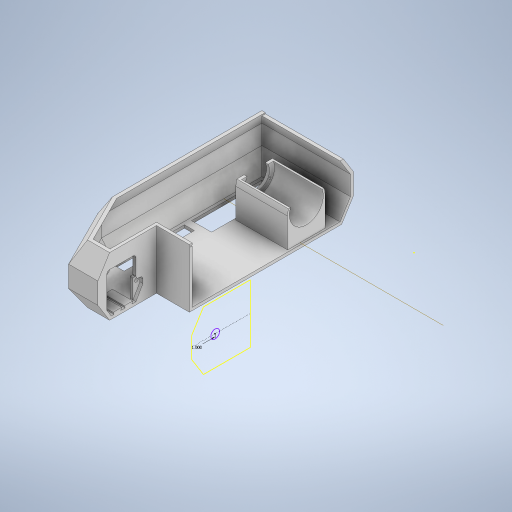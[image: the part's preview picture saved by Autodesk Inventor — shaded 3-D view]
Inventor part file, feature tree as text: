
AUTODESK INVENTOR PART (.ipt)
format: ipt  version: 2024 (Build 280153000, 153)  size: 1,161,216 bytes
history: native  units: in
note: dims shown in document units (in); Inventor stores cm internally (conversion verified against a paired STEP export)
features: extrude x14, sketch x13, projected_geometry x12, fillet x3, chamfer x2, shell x1, other x1, plane x1, mirror x1, hole x1
ambient origin geometry x8: Origin, YZ Plane, XZ Plane, XY Plane, X Axis, Y Axis, Z Axis, Center Point
bodies: Solid1 (feature_tree)
feature tree (49):
  extrude  "Extrusion1"  Depth=0.8in
  chamfer  "Chamfer1"  Distance=2.5in
  chamfer  "Chamfer2"  Distance=0.5in Angle=30.0deg
  shell  "Shell1"  Thickness=0.125in
  extrude  "Extrusion2"  Depth=3.0in
  extrude  "Extrusion3"  Depth=0.125in
  sketch  "Sketch4"  dims[d17=3.0in d18=0.125in]
  extrude  "Extrusion4"  Depth=0.125in
  extrude  "Extrusion5"  Depth=0.425in TaperAngle=0.0deg
  other  "Work Axis1"
  extrude  "Extrusion6"  Depth=0.125in
  plane  "Work Plane1"
  extrude  "Extrusion7"  Depth=0.125in TaperAngle=0.0deg
  extrude  "Extrusion8"  Depth=0.0625in
  mirror  "Mirror1"
  extrude  "Extrusion12"  Depth=0.0625in TaperAngle=0.0deg
  fillet  "Fillet1"  Radius=0.0625in
  extrude  "Extrusion13"  Depth=2.08in
  sketch  "Sketch15"  dims[d36=1.6in d38=2.08in]
  extrude  "Extrusion14"  Depth=1.5in
  fillet  "Fillet2"  Radius=1.5in
  extrude  "Extrusion15"  Depth=0.125in TaperAngle=0.0deg
  fillet  "Fillet3"  Radius=1.25in
  sketch  "Sketch16"  dims[d39=0.2in d40=0.268in d41=1.5in]
  hole  "Hole1"  [1 undecoded]
  extrude  "Extrusion16"  Depth=0.125in
  extrude  "Extrusion9"  Depth=0.125in
  sketch  "Sketch1"  dims[d4=1.25in d5=1.25in d6=2.5in d7=0.0in d8=0.5in d9=0.8in d10=30.0deg]
  sketch  "Sketch2"  dims[d11=0.5in d12=0.8in d13=60.0deg d14=0.125in]
  projected_geometry  "Projected Loop1"
  sketch  "Sketch3"  dims[d15=0.85in d16=3.0in]
  projected_geometry  "Projected Loop2"
  projected_geometry  "Projected Loop3"
  projected_geometry  "Projected Loop4"
  sketch  "Sketch5"  dims[d19=0.125in d20=0.125in]
  sketch  "Sketch6"  dims[d21=0.425in d22=1.0in d23=0.0in]
  projected_geometry  "Projected Loop5"
  sketch  "Sketch7"  dims[d24=0.125in d25=0.125in]
  projected_geometry  "Projected Loop6"
  sketch  "Sketch8"  dims[d26=0.125in d27=1.0in d28=0.0in]
  projected_geometry  "Projected Loop7"
  sketch  "Sketch12"  dims[d29=0.0625in d30=0.0625in]
  projected_geometry  "Projected Loop13"
  projected_geometry  "Projected Loop14"
  sketch  "Sketch13"  dims[d31=0.0625in d32=0.0625in d33=0.0in d34=0.0625in d35=0.0in]
  projected_geometry  "Projected Loop15"
  projected_geometry  "Projected Loop17"
  projected_geometry  "Projected Loop18"
  sketch  "Sketch17"  dims[d42=0.0in d44=5.6in d45=0.0in d46=1.25in d47=1.45in d49=0.21in d50=1.45in d51=0.09in d52=0.07in d53=2.3622in d55=360.0deg d57=0.125in d58=0.0in d60=1.0in d61=1.0336in d62=0.31in d63=45.0deg d64=0.6425in d65=1.5748in d67=360.0deg d69=1.0in d70=0.0in d80=1.245in d81=1.0in d83=1.75in d84=1.0in d85=0.0in d86=0.125in d87=0.3081in d88=0.3in d89=0.1in d90=0.375in d91=0.1in d92=0.1in d93=0.005in d94=0.005in d95=0.005in d96=0.005in d97=0.005in d98=0.005in d99=0.8661in d100=0.0in d107=0.3in d108=0.3in d109=30.0deg d110=0.125in d112=0.15in d113=1.0in d114=0.0in d115=0.125in d116=0.0in d117=0.125in d118=0.125in d122=0.771in d123=1.0in d124=0.1575in d125=0.75in d126=0.417in d127=0.118in d128=90.0deg d129=0.125in d130=0.0in d131=8.3125in d132=0.5935in d133=0.0in d134=0.0in]
note: 1 required parameter value undecoded (feature->parameter linkage not recoverable at this tier; creation-order binding heuristic only, values carry confidence <= 0.55)
